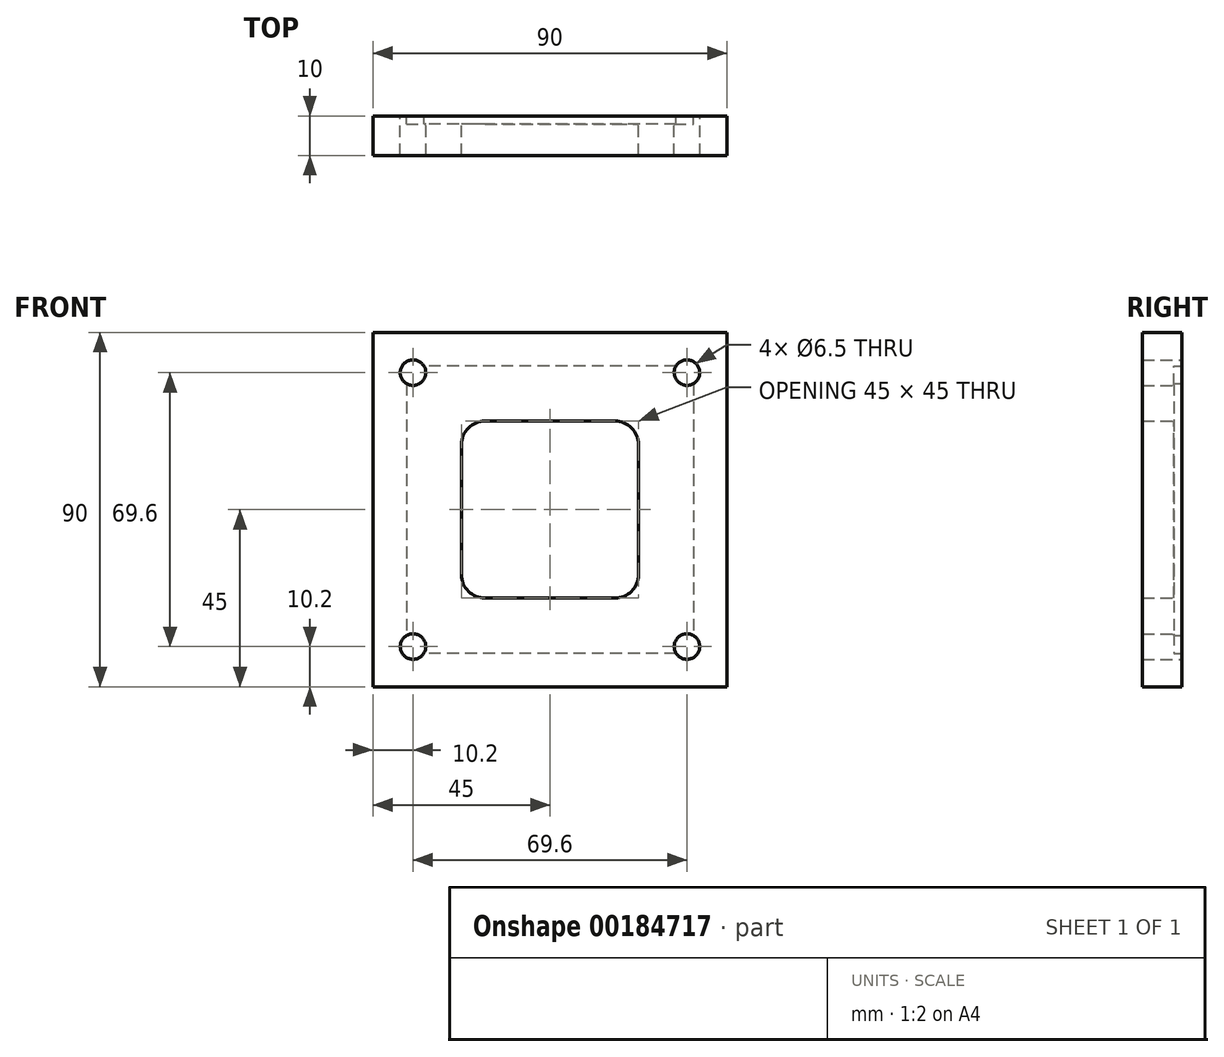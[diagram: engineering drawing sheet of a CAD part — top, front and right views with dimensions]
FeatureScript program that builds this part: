
annotation { "Feature Type Name" : "Feature", "Feature Type Description" : "" }
export const myFeature = defineFeature(function(context is Context, id is Id, definition is map)
    precondition{}
    {
        {
            var Q0;
            Q0=qCreatedBy(makeId("Front.planeOp"),FACE);
            var sketch = newSketch(context, id + "F0", { "sketchPlane" : qUnion([Q0])});
            skLineSegment(sketch, "E0.bottom", {"start": v(-45, 45) * mm, "end": v(45, 45) * mm});
            skLineSegment(sketch, "E0.top", {"start": v(-45, -45) * mm, "end": v(45, -45) * mm});
            skLineSegment(sketch, "E0.left", {"start": v(-45, 45) * mm, "end": v(-45, -45) * mm});
            skLineSegment(sketch, "E0.right", {"start": v(45, 45) * mm, "end": v(45, -45) * mm});
            skCircle(sketch, "E1", {"center": v(-34.8, 34.8) * mm, "radius": 3.25 * mm});
            skCircle(sketch, "E2.MirrorC", {"center": v(-34.8, -34.8) * mm, "radius": 3.25 * mm});
            skCircle(sketch, "E3.MirrorC", {"center": v(34.8, -34.8) * mm, "radius": 3.25 * mm});
            skCircle(sketch, "E4.MirrorC", {"center": v(34.8, 34.8) * mm, "radius": 3.25 * mm});
            skSolve(sketch);
        }
        {
            var Q0;
            Q0 = qSketchRegion(id + "F0", true);
            extrude(context, id + "F1", {"entities" : qUnion([Q0]), "depth" : 10 * mm});
        }
        {
            var Q0;
            Q0=qCreatedBy(makeId("Front.planeOp"),FACE);
            var sketch = newSketch(context, id + "F2", { "sketchPlane" : qUnion([Q0])});
            skLineSegment(sketch, "E5.bottom", {"start": v(32.5, 36.5) * mm, "end": v(-32.5, 36.5) * mm});
            skLineSegment(sketch, "E5.top", {"start": v(32.5, -36.5) * mm, "end": v(-32.5, -36.5) * mm});
            skLineSegment(sketch, "E5.left", {"start": v(36.5, 32.5) * mm, "end": v(36.5, -32.5) * mm});
            skLineSegment(sketch, "E5.right", {"start": v(-36.5, 32.5) * mm, "end": v(-36.5, -32.5) * mm});
            skPoint(sketch, "E6.visualSharp", {"position": v(36.5, 36.5) * mm});
            skArc(sketch, "E6.filletArc", {"start": v(36.5, 32.5) * mm, "mid": v(35.33, 35.33) * mm, "end": v(32.5, 36.5) * mm});
            skPoint(sketch, "E7.visualSharp", {"position": v(-36.5, 36.5) * mm});
            skArc(sketch, "E7.filletArc", {"start": v(-32.5, 36.5) * mm, "mid": v(-35.33, 35.33) * mm, "end": v(-36.5, 32.5) * mm});
            skPoint(sketch, "E8.visualSharp", {"position": v(-36.5, -36.5) * mm});
            skArc(sketch, "E8.filletArc", {"start": v(-36.5, -32.5) * mm, "mid": v(-35.33, -35.33) * mm, "end": v(-32.5, -36.5) * mm});
            skPoint(sketch, "E9.visualSharp", {"position": v(36.5, -36.5) * mm});
            skArc(sketch, "E9.filletArc", {"start": v(32.5, -36.5) * mm, "mid": v(35.33, -35.33) * mm, "end": v(36.5, -32.5) * mm});
            skSolve(sketch);
        }
        {
            var Q0;
            Q0 = qSketchRegion(id + "F2", true);
            extrude(context, id + "F3", {"entities" : qUnion([Q0]), "operationType" : NewBodyOperationType.REMOVE, "depth" : 2 * mm});
        }
        {
            var Q0;
            Q0=qCreatedBy(makeId("Front.planeOp"),FACE);
            var sketch = newSketch(context, id + "F4", { "sketchPlane" : qUnion([Q0])});
            skLineSegment(sketch, "E10.bottom", {"start": v(16.5, 22.5) * mm, "end": v(-16.5, 22.5) * mm});
            skLineSegment(sketch, "E10.top", {"start": v(16.5, -22.5) * mm, "end": v(-16.5, -22.5) * mm});
            skLineSegment(sketch, "E10.left", {"start": v(22.5, 16.5) * mm, "end": v(22.5, -16.5) * mm});
            skLineSegment(sketch, "E10.right", {"start": v(-22.5, 16.5) * mm, "end": v(-22.5, -16.5) * mm});
            skPoint(sketch, "E10.middle", {"position": v(0, 0) * mm});
            skPoint(sketch, "E11.visualSharp", {"position": v(-22.5, 22.5) * mm});
            skArc(sketch, "E11.filletArc", {"start": v(-16.5, 22.5) * mm, "mid": v(-20.74, 20.74) * mm, "end": v(-22.5, 16.5) * mm});
            skPoint(sketch, "E12.visualSharp", {"position": v(22.5, 22.5) * mm});
            skArc(sketch, "E12.filletArc", {"start": v(22.5, 16.5) * mm, "mid": v(20.74, 20.74) * mm, "end": v(16.5, 22.5) * mm});
            skPoint(sketch, "E13.visualSharp", {"position": v(22.5, -22.5) * mm});
            skArc(sketch, "E13.filletArc", {"start": v(16.5, -22.5) * mm, "mid": v(20.74, -20.74) * mm, "end": v(22.5, -16.5) * mm});
            skPoint(sketch, "E14.visualSharp", {"position": v(-22.5, -22.5) * mm});
            skArc(sketch, "E14.filletArc", {"start": v(-22.5, -16.5) * mm, "mid": v(-20.74, -20.74) * mm, "end": v(-16.5, -22.5) * mm});
            skSolve(sketch);
        }
        {
            var Q0;
            Q0 = qSketchRegion(id + "F4", true);
            extrude(context, id + "F5", {"entities" : qUnion([Q0]), "operationType" : NewBodyOperationType.REMOVE, "endBound" : BoundingType.THROUGH_ALL, "depth" : 25 * mm});
        }
    });
